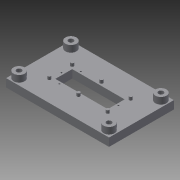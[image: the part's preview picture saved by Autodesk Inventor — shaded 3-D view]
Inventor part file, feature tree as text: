
AUTODESK INVENTOR PART (.ipt)
format: ipt  version: 2015 (Build 190159000, 159)  size: 167,936 bytes
history: native  units: in
note: dims shown in document units (in); Inventor stores cm internally (conversion verified against a paired STEP export)
features: extrude x4, sketch x2
ambient origin geometry x8: Origin, YZ Plane, XZ Plane, XY Plane, X Axis, Y Axis, Z Axis, Center Point
bodies: Solid1 (feature_tree)
feature tree (6):
  extrude  "Extrusion1"  Depth=2.6575in
  extrude  "Extrusion2"  Depth=0.0394in
  extrude  "Extrusion4"  Depth=0.4354in
  extrude  "Extrusion5"  Depth=0.4354in
  sketch  "Sketch1"  dims[d0=1.6732in d1=2.6575in]
  sketch  "Sketch5"  dims[d2=0.2091in d3=0.0in d4=0.0394in d15=0.5535in d23=1.4701in d31=0.1181in d32=0.0in d39=0.2217in d59=0.0787in d60=0.0in d69=0.1181in d70=0.1673in d79=0.128in d82=0.0394in d83=0.0394in d84=0.0394in d85=0.0394in d90=0.1673in d91=0.1673in d92=0.0787in d93=1.3386in d94=2.3228in d95=0.0787in d96=0.0787in d97=0.0787in d98=0.0906in d99=0.0in d100=0.4354in]
